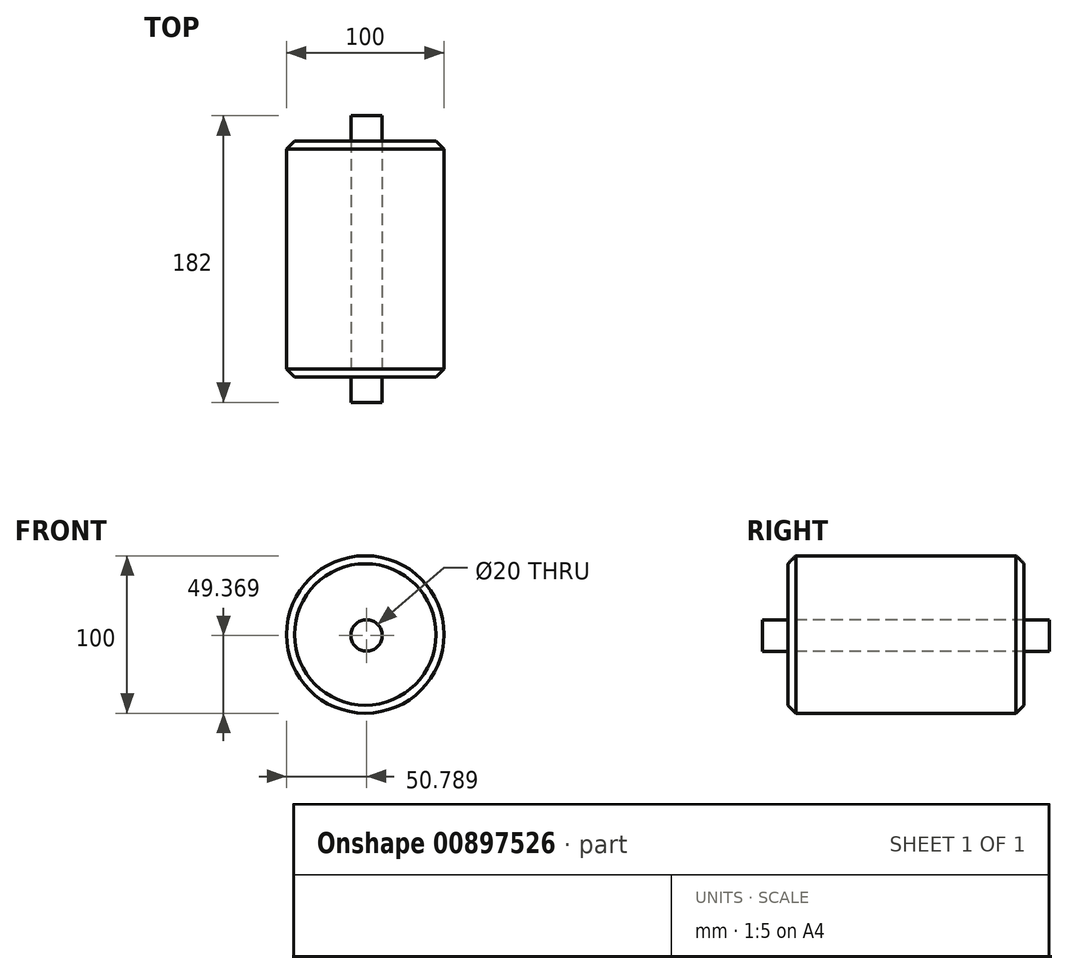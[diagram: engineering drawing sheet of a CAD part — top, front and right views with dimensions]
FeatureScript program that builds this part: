
annotation { "Feature Type Name" : "Feature", "Feature Type Description" : "" }
export const myFeature = defineFeature(function(context is Context, id is Id, definition is map)
    precondition{}
    {
        {
            var Q0;
            Q0=qCreatedBy(makeId("Front.planeOp"),FACE);
            var sketch = newSketch(context, id + "F0", { "sketchPlane" : qUnion([Q0])});
            skCircle(sketch, "E0", {"center": v(0.79, -0.63) * mm, "radius": 10 * mm});
            skSolve(sketch);
        }
        {
            var Q0;
            Q0=makeQuery(id+"F0.imprint","IMPRINT",FACE,{"disambiguationData":[TD([[makeQuery(id+"F0.imprint","IMPRINT",EDGE,{"derivedFrom":sQuery(id+"F0.wireOp",EDGE,"E0")}),1.0]])]});
            extrude(context, id + "F1", {"entities" : qUnion([Q0]), "depth" : 16 * mm, "offsetDistance" : 25.4 * mm});
        }
        {
            var Q0;
            Q0=makeQuery(id+"F1.opExtrude","CAP_FACE",FACE,{"disambiguationData":[OSD([sQuery(id+"F0.wireOp",EDGE,"E0")])],"isStart":true});
            var sketch = newSketch(context, id + "F2", { "sketchPlane" : qUnion([Q0])});
            skCircle(sketch, "E1", {"center": v(0, 0) * mm, "radius": 50 * mm});
            skSolve(sketch);
        }
        {
            var Q0;
            Q0=makeQuery(id+"F2.imprint","IMPRINT",FACE,{"disambiguationData":[TD([[makeQuery(id+"F2.imprint","IMPRINT",EDGE,{"derivedFrom":sQuery(id+"F2.wireOp",EDGE,"E1")}),1.0]])]});
            extrude(context, id + "F3", {"entities" : qUnion([Q0]), "depth" : 150 * mm, "offsetDistance" : 25.4 * mm});
        }
        {
            var Q0;
            Q0=makeQuery(id+"F3.opExtrude","CAP_FACE",FACE,{"disambiguationData":[OSD([sQuery(id+"F0.wireOp",EDGE,"E0"),sQuery(id+"F2.wireOp",EDGE,"E1")])],"isStart":false});
            var sketch = newSketch(context, id + "F4", { "sketchPlane" : qUnion([Q0])});
            skSolve(sketch);
        }
        {
            var Q0;
            Q0=makeQuery(id+"F4.imprint","IMPRINT",FACE,{"disambiguationData":[TD([[makeQuery(id+"F4.imprint","IMPRINT",EDGE,{"derivedFrom":makeQuery(id+"F3.opExtrude","CAP_EDGE",EDGE,{"disambiguationData":[OSD([sQuery(id+"F2.wireOp",EDGE,"E1")])],"isStart":false})}),1.0]])]});
            var sketch = newSketch(context, id + "F5", { "sketchPlane" : qUnion([Q0])});
            skCircle(sketch, "E2", {"center": v(0, 0) * mm, "radius": 11.01 * mm});
            skSolve(sketch);
        }
        {
            var Q0;
            Q0=makeQuery(id+"F5.imprint","IMPRINT",FACE,{"disambiguationData":[TD([[makeQuery(id+"F5.imprint","IMPRINT",EDGE,{"derivedFrom":makeQuery(id+"F4.imprint","IMPRINT",EDGE,{"derivedFrom":makeQuery(id+"F3.opExtrude","CAP_EDGE",EDGE,{"disambiguationData":[OSD([sQuery(id+"F0.wireOp",EDGE,"E0")])],"isStart":false})})}),-1.0]])]});
            var Q1;
            Q1=sQuery(id+"F5.wireOp",EDGE,"E2");
            extrude(context, id + "F6", {"entities" : qUnion([Q0]), "surfaceEntities" : qUnion([Q1]), "depth" : 16 * mm, "offsetDistance" : 25.4 * mm});
        }
        {
            var Q0;
            Q0=makeQuery(id+"F3.opExtrude","CAP_EDGE",EDGE,{"disambiguationData":[OSD([sQuery(id+"F2.wireOp",EDGE,"E1")])],"isStart":false});
            var Q1;
            Q1=makeQuery(id+"F3.opExtrude","CAP_EDGE",EDGE,{"disambiguationData":[OSD([sQuery(id+"F2.wireOp",EDGE,"E1")])],"isStart":true});
            chamfer(context, id + "F7", {"entities" : qUnion([Q0, Q1]), "width" : 5.08 * mm, "tangentPropagation" : true});
        }
    });
